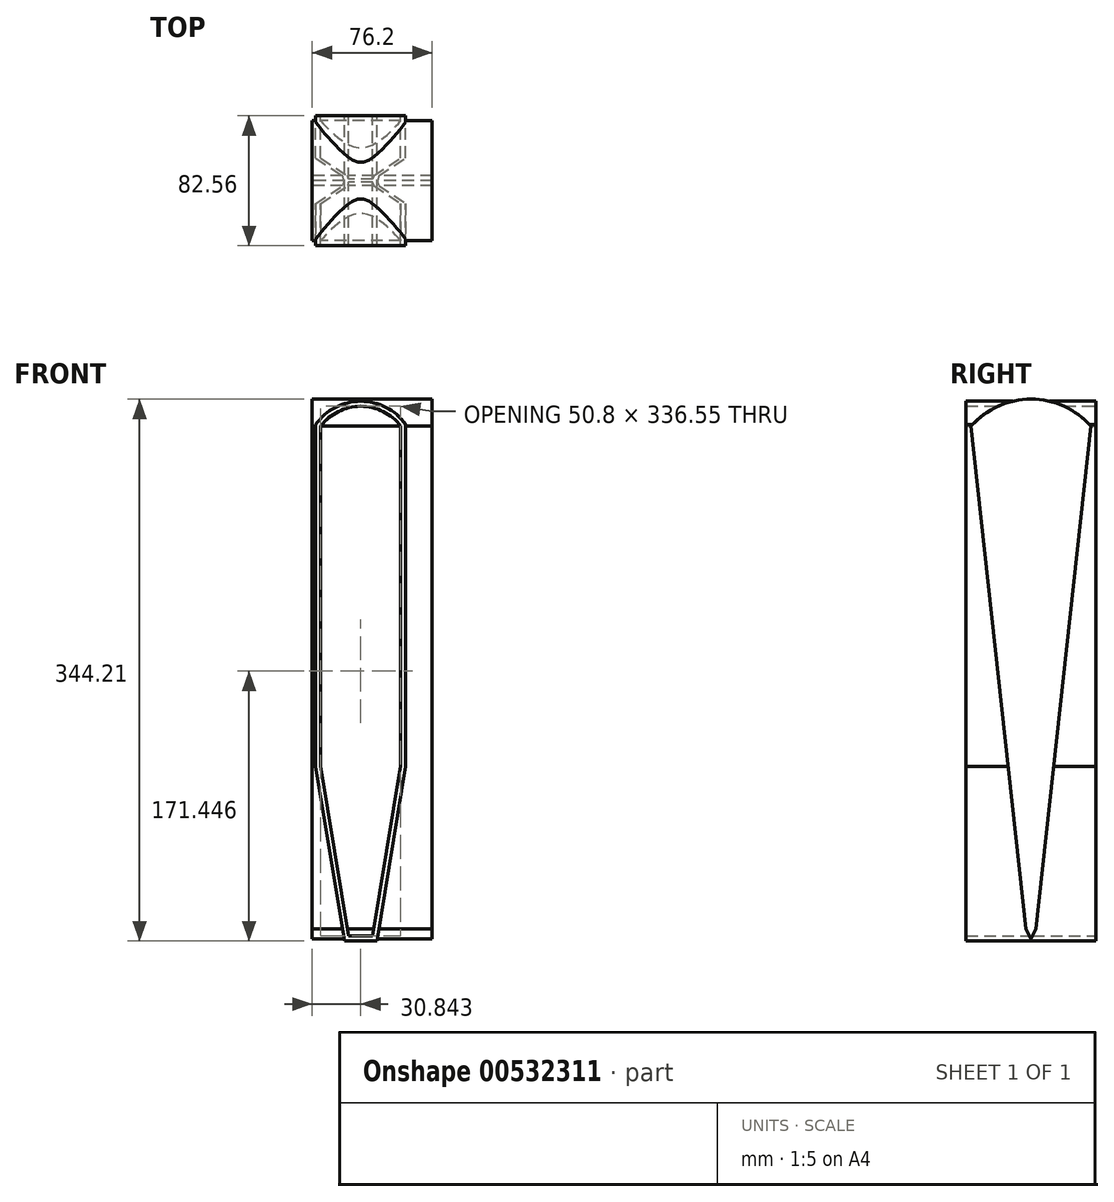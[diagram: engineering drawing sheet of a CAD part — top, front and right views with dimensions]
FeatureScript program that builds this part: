
annotation { "Feature Type Name" : "Feature", "Feature Type Description" : "" }
export const myFeature = defineFeature(function(context is Context, id is Id, definition is map)
    precondition{}
    {
        {
            var Q0;
            Q0=qCreatedBy(makeId("Front.planeOp"),FACE);
            var sketch = newSketch(context, id + "F0", { "sketchPlane" : qUnion([Q0])});
            skLineSegment(sketch, "E0", {"start": v(56.24, 0.28) * mm, "end": v(56.24, -215.62) * mm});
            skLineSegment(sketch, "E1", {"start": v(5.44, 0.28) * mm, "end": v(5.44, -215.62) * mm});
            skLineSegment(sketch, "E2", {"start": v(56.24, 0.28) * mm, "end": v(5.44, 0.28) * mm, "construction": true});
            skLineSegment(sketch, "E3", {"start": v(56.24, -215.62) * mm, "end": v(38.46, -323.57) * mm});
            skLineSegment(sketch, "E4", {"start": v(38.46, -323.57) * mm, "end": v(23.22, -323.57) * mm});
            skLineSegment(sketch, "E5", {"start": v(23.22, -323.57) * mm, "end": v(5.44, -215.62) * mm});
            skLineSegment(sketch, "E6", {"start": v(30.84, -323.57) * mm, "end": v(30.84, 0.28) * mm, "construction": true});
            skArc(sketch, "E7", {"start": v(56.24, 0.28) * mm, "mid": v(30.84, 12.98) * mm, "end": v(5.44, 0.28) * mm});
            skLineSegment(sketch, "E8", {"start": v(30.84, 0.28) * mm, "end": v(30.84, 12.98) * mm, "construction": true});
            skArc(sketch, "E9.0", {"start": v(59.42, 1.31) * mm, "mid": v(30.84, 16.16) * mm, "end": v(2.27, 1.31) * mm});
            skLineSegment(sketch, "E9.1", {"start": v(20.53, -326.74) * mm, "end": v(2.27, -215.88) * mm});
            skLineSegment(sketch, "E9.2", {"start": v(41.16, -326.74) * mm, "end": v(20.53, -326.74) * mm});
            skLineSegment(sketch, "E9.3", {"start": v(2.27, 1.31) * mm, "end": v(2.27, -215.88) * mm});
            skLineSegment(sketch, "E9.4", {"start": v(59.42, -215.88) * mm, "end": v(41.16, -326.74) * mm});
            skLineSegment(sketch, "E9.5", {"start": v(59.42, 1.31) * mm, "end": v(59.42, -215.88) * mm});
            skSolve(sketch);
        }
        {
            var Q0;
            Q0=qCreatedBy(makeId("Right.planeOp"),FACE);
            var sketch = newSketch(context, id + "F1", { "sketchPlane" : qUnion([Q0])});
            skLineSegment(sketch, "E10", {"start": v(-3.18, -319.08) * mm, "end": v(-38.1, 0.28) * mm});
            skLineSegment(sketch, "E11", {"start": v(3.17, -319.08) * mm, "end": v(38.1, 0.28) * mm});
            skArc(sketch, "E12", {"start": v(38.1, 0.28) * mm, "mid": v(0, 17.47) * mm, "end": v(-38.1, 0.28) * mm});
            skLineSegment(sketch, "E13", {"start": v(-38.1, 0.28) * mm, "end": v(38.1, 0.28) * mm});
            skLineSegment(sketch, "E14", {"start": v(-38.1, 0.28) * mm, "end": v(-2.46, 0.28) * mm, "construction": true});
            skLineSegment(sketch, "E15", {"start": v(-2.46, 0.28) * mm, "end": v(38.1, 0.28) * mm, "construction": true});
            skLineSegment(sketch, "E16", {"start": v(-3.18, -319.08) * mm, "end": v(0, -319.08) * mm, "construction": true});
            skLineSegment(sketch, "E17", {"start": v(0, -319.08) * mm, "end": v(3.17, -319.08) * mm, "construction": true});
            skLineSegment(sketch, "E18", {"start": v(-3.18, -319.08) * mm, "end": v(0, -325.43) * mm});
            skLineSegment(sketch, "E19", {"start": v(3.17, -319.08) * mm, "end": v(0, -325.43) * mm});
            skLineSegment(sketch, "E20", {"start": v(0, -319.08) * mm, "end": v(0, -325.43) * mm, "construction": true});
            skLineSegment(sketch, "E21", {"start": v(0, -325.43) * mm, "end": v(0, 17.47) * mm, "construction": true});
            skPoint(sketch, "E22", {"position": v(0, 0.28) * mm});
            skSolve(sketch);
        }
        {
            var Q0;
            Q0=makeQuery(id+"F1.imprint","IMPRINT",FACE,{"disambiguationData":[TD([[makeQuery(id+"F1.imprint","IMPRINT",EDGE,{"derivedFrom":sQuery(id+"F1.wireOp",EDGE,"E10")}),-1.0]])]});
            var Q1;
            Q1=makeQuery(id+"F1.imprint","IMPRINT",FACE,{"disambiguationData":[TD([[makeQuery(id+"F1.imprint","IMPRINT",EDGE,{"derivedFrom":sQuery(id+"F1.wireOp",EDGE,"E12")}),1.0]])]});
            extrude(context, id + "F2", {"entities" : qUnion([Q0, Q1]), "depth" : 76.2 * mm});
        }
        {
            var Q0;
            Q0=makeQuery(id+"F0.imprint","IMPRINT",FACE,{"disambiguationData":[TD([[makeQuery(id+"F0.imprint","IMPRINT",EDGE,{"derivedFrom":sQuery(id+"F0.wireOp",EDGE,"E0")}),1.0]])]});
            extrude(context, id + "F3", {"entities" : qUnion([Q0]), "operationType" : NewBodyOperationType.ADD, "depth" : 82.55 * mm, "symmetric" : true});
        }
    });
